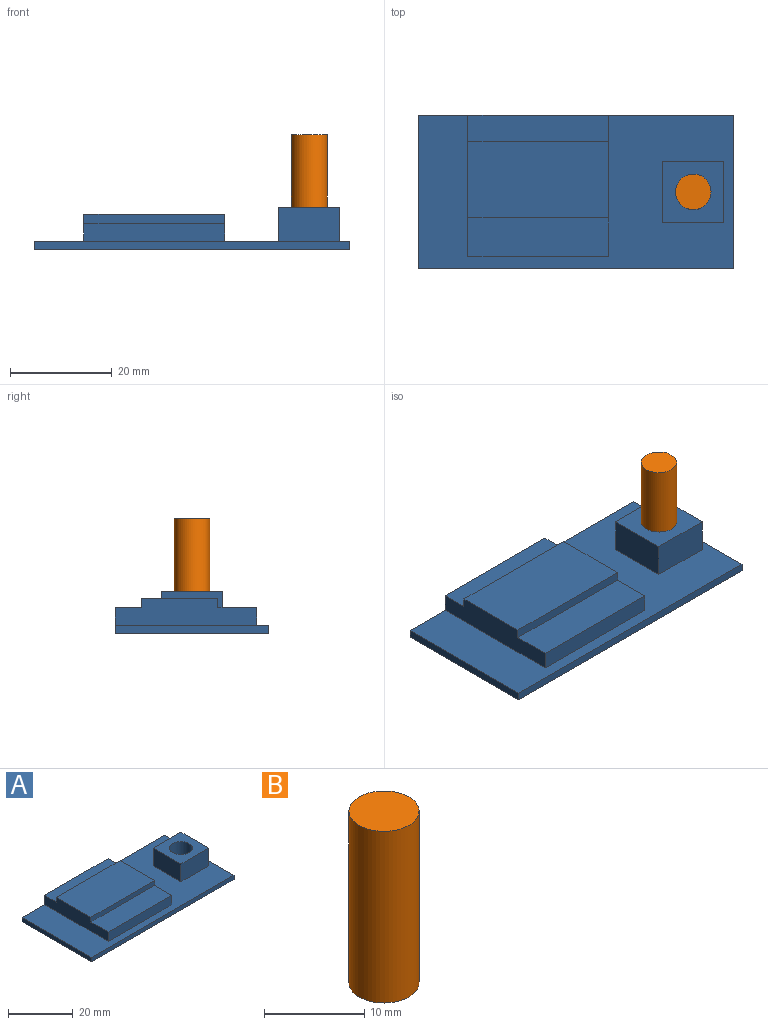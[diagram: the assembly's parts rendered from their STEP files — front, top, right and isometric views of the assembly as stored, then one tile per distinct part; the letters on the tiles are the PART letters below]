
ASSEMBLY  parts=2 mates=1
PART A: 21 faces, bbox 62.1x30.2x8.3 mm
  f0: plane 27.7x7.6mm, normal (0,0,1), area 210.5mm2, adj f14,f15,f16,f18
  f1: plane 30.2x1.6mm, normal (1,0,0), area 48.3mm2, adj f2,f4,f5,f6
  f2: plane 62.1x5.1mm, normal (0,1,0), area 196.3mm2, adj f1,f3,f5,f6,f14,f16,f17
  f3: plane 30.2x1.6mm, normal (-1,0,0), area 48.3mm2, adj f2,f4,f5,f6
  f4: plane 62.1x1.6mm, normal (0,-1,0), area 99.4mm2, adj f1,f3,f5,f6
  f5: plane 62.1x30.2mm, normal (0,0,1), area 961.4mm2, adj f1,f2,f3,f4,f7,f8,f9,f11
  f6: plane 62.1x30.2mm, normal (0,0,-1), area 1875.4mm2, adj f1,f2,f3,f4
  f7: plane 12x6.7mm, normal (0,1,0), area 80.4mm2, adj f5,f8,f11,f12
  f8: plane 12x6.7mm, normal (-1,0,0), area 80.4mm2, adj f5,f7,f9,f12
  f9: plane 12x6.7mm, normal (0,-1,0), area 80.4mm2, adj f5,f8,f11,f12
  f10: cylinder r=3.5mm len=7mm, axis (0,0,-1), area 147.3mm2, adj f12,f13
  f11: plane 12x6.7mm, normal (1,0,0), area 80.4mm2, adj f5,f7,f9,f12
  f12: plane 12x12mm, normal (0,0,1), area 105.5mm2, adj f7,f8,f9,f10,f11
  f13: plane 7x7mm, normal (0,0,1), area 38.5mm2, adj f10
  f14: plane 27.8x5.3mm, normal (-1,0,0), area 124.3mm2, adj f0,f2,f5,f15,f17,f18,f19,f20
  f15: plane 27.7x3.5mm, normal (0,-1,0), area 96.9mm2, adj f0,f5,f14,f16
  f16: plane 27.8x5.3mm, normal (1,0,0), area 124.3mm2, adj f0,f2,f5,f15,f17,f18,f19,f20
  f17: plane 27.7x5.2mm, normal (0,0,1), area 144mm2, adj f2,f14,f16,f19
  f18: plane 27.7x1.8mm, normal (0,-1,0), area 49.9mm2, adj f0,f14,f16,f20
  f19: plane 27.7x1.8mm, normal (0,1,0), area 49.9mm2, adj f14,f16,f17,f20
  f20: plane 27.7x15mm, normal (0,0,1), area 415.5mm2, adj f14,f16,f18,f19
PART B: 3 faces, bbox 7x7x21 mm
  f0: cylinder r=3.5mm len=21mm, axis (0,0,-1), area 461.8mm2, adj f1,f2
  f1: plane 7x7mm, normal (0,0,1), area 38.5mm2, adj f0
  f2: plane 7x7mm, normal (0,0,-1), area 38.5mm2, adj f0
PLACE A at identity
PLACE B at identity
MATE fastened B.f0 <-> A.f10  axis (0,0,-1) through (54.1,15.1,1.6)mm
